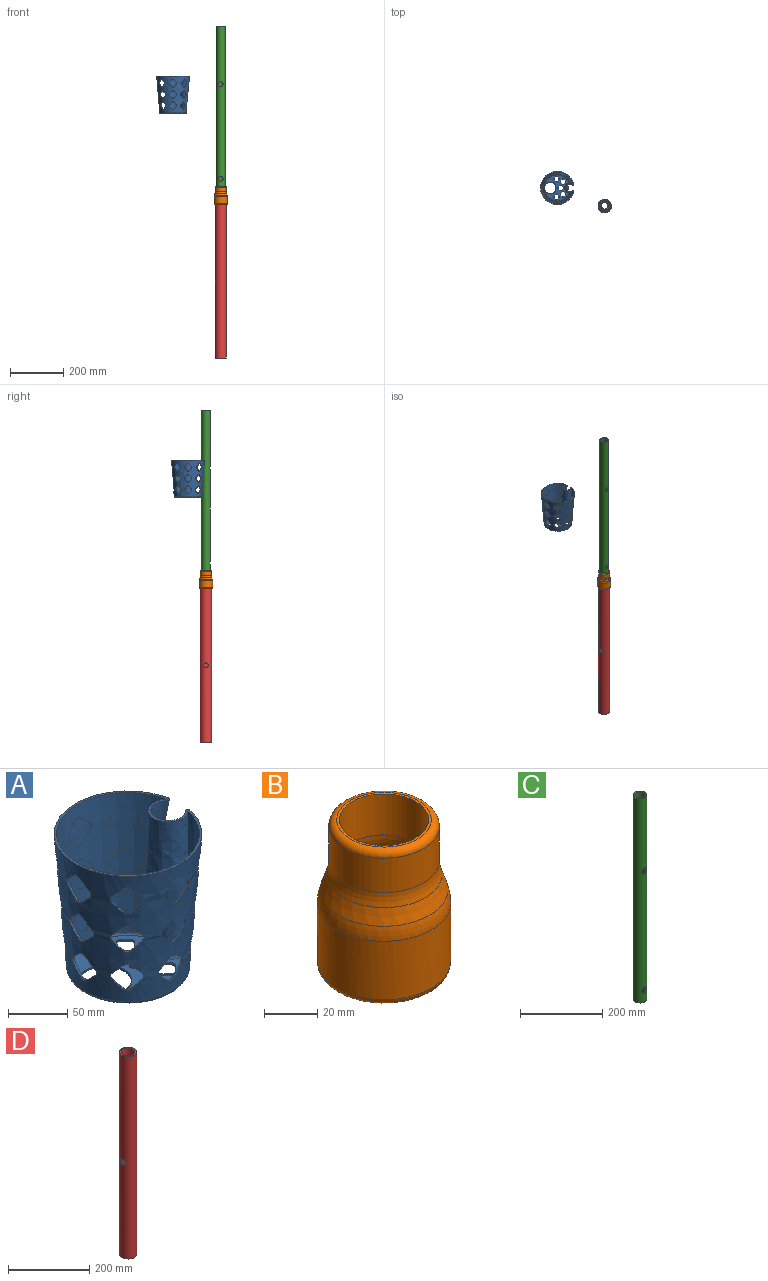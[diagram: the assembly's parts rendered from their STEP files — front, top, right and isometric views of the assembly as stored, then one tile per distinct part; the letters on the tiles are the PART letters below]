
ASSEMBLY  parts=4 mates=2
PART A: 242 faces, bbox 129.3x129x156.7 mm
  f0: plane 97.9x93.66mm, normal (0,0,-1), area 4142.3mm2, adj f1,f2,f3,f4,f5,f6,f7,f8
  f1: plane 7.07x7.07mm, normal (-0.71,-0.71,0), area 20mm2, adj f0,f2,f8,f45
  f2: cylinder r=3mm len=4.24mm, axis (0,0,1), area 9.4mm2, adj f0,f1,f3,f45
  f3: plane 7.07x7.07mm, normal (0.71,-0.71,0), area 20mm2, adj f0,f2,f4,f45
  f4: cylinder r=3mm len=4.24mm, axis (0,0,1), area 9.4mm2, adj f0,f3,f5,f45
  f5: plane 7.07x7.07mm, normal (0.71,0.71,0), area 20mm2, adj f0,f4,f6,f45
  f6: cylinder r=3mm len=4.24mm, axis (0,0,1), area 9.4mm2, adj f0,f5,f7,f45
  f7: plane 7.07x7.07mm, normal (-0.71,0.71,0), area 20mm2, adj f0,f6,f8,f45
  f8: cylinder r=3mm len=4.24mm, axis (0,0,1), area 9.4mm2, adj f0,f1,f7,f45
  f9: plane 7.07x7.07mm, normal (-0.71,-0.71,0), area 20mm2, adj f0,f10,f16,f45
  f10: cylinder r=3mm len=4.24mm, axis (0,0,1), area 9.4mm2, adj f0,f9,f11,f45
  f11: plane 7.07x7.07mm, normal (0.71,-0.71,0), area 20mm2, adj f0,f10,f12,f45
  f12: cylinder r=3mm len=4.24mm, axis (0,0,1), area 9.4mm2, adj f0,f11,f13,f45
  f13: plane 7.07x7.07mm, normal (0.71,0.71,0), area 20mm2, adj f0,f12,f14,f45
  f14: cylinder r=3mm len=4.24mm, axis (0,0,1), area 9.4mm2, adj f0,f13,f15,f45
  f15: plane 7.07x7.07mm, normal (-0.71,0.71,0), area 20mm2, adj f0,f14,f16,f45
  f16: cylinder r=3mm len=4.24mm, axis (0,0,1), area 9.4mm2, adj f0,f9,f15,f45
  f17: plane 7.07x7.07mm, normal (-0.71,-0.71,0), area 20mm2, adj f0,f18,f24,f45
  f18: cylinder r=3mm len=4.24mm, axis (0,0,1), area 9.4mm2, adj f0,f17,f19,f45
  f19: plane 7.07x7.07mm, normal (0.71,-0.71,0), area 20mm2, adj f0,f18,f20,f45
  f20: cylinder r=3mm len=4.24mm, axis (0,0,1), area 9.4mm2, adj f0,f19,f21,f45
  f21: plane 7.07x7.07mm, normal (0.71,0.71,0), area 20mm2, adj f0,f20,f22,f45
  f22: cylinder r=3mm len=4.24mm, axis (0,0,1), area 9.4mm2, adj f0,f21,f23,f45
  f23: plane 7.07x7.07mm, normal (-0.71,0.71,0), area 20mm2, adj f0,f22,f24,f45
  f24: cylinder r=3mm len=4.24mm, axis (0,0,1), area 9.4mm2, adj f0,f17,f23,f45
  f25: torus R=48.95mm, axis (0,0,1), area 1245.7mm2, adj f0,f46,f47,f48
  f26: bspline ~24.16x19.79mm, area 116.1mm2, adj f0,f46,f49,f50,f51,f52
  f27: bspline ~20.75x19.05mm, area 115.6mm2, adj f0,f48,f49,f51,f53,f54
  f28: cylinder r=22mm len=44mm, axis (0,0,1), area 276.5mm2, adj f0,f45
  f29: plane 7.07x7.07mm, normal (-0.71,-0.71,0), area 20mm2, adj f0,f30,f36,f45
  f30: cylinder r=3mm len=4.24mm, axis (0,0,1), area 9.4mm2, adj f0,f29,f31,f45
  f31: plane 7.07x7.07mm, normal (0.71,-0.71,0), area 20mm2, adj f0,f30,f32,f45
  f32: cylinder r=3mm len=4.24mm, axis (0,0,1), area 9.4mm2, adj f0,f31,f33,f45
  f33: plane 7.07x7.07mm, normal (0.71,0.71,0), area 20mm2, adj f0,f32,f34,f45
  f34: cylinder r=3mm len=4.24mm, axis (0,0,1), area 9.4mm2, adj f0,f33,f35,f45
  f35: plane 7.07x7.07mm, normal (-0.71,0.71,0), area 20mm2, adj f0,f34,f36,f45
  f36: cylinder r=3mm len=4.24mm, axis (0,0,1), area 9.4mm2, adj f0,f29,f35,f45
  f37: plane 7.07x7.07mm, normal (-0.71,-0.71,0), area 20mm2, adj f0,f38,f44,f45
  f38: cylinder r=3mm len=4.24mm, axis (0,0,1), area 9.4mm2, adj f0,f37,f39,f45
  f39: plane 7.07x7.07mm, normal (0.71,-0.71,0), area 20mm2, adj f0,f38,f40,f45
  f40: cylinder r=3mm len=4.24mm, axis (0,0,1), area 9.4mm2, adj f0,f39,f41,f45
  f41: plane 7.07x7.07mm, normal (0.71,0.71,0), area 20mm2, adj f0,f40,f42,f45
  f42: cylinder r=3mm len=4.24mm, axis (0,0,1), area 9.4mm2, adj f0,f41,f43,f45
  f43: plane 7.07x7.07mm, normal (-0.71,0.71,0), area 20mm2, adj f0,f42,f44,f45
  f44: cylinder r=3mm len=4.24mm, axis (0,0,1), area 9.4mm2, adj f0,f37,f43,f45
  f45: plane 97.9x93.65mm, normal (0,0,1), area 4142.6mm2, adj f1,f2,f3,f4,f5,f6,f7,f8
  f46: bspline ~3.42x2.81mm, area 7.8mm2, adj f25,f26,f52
  f47: cone r=62.5mm half-angle=4.4deg, axis (0,0,1), area 33496mm2, adj f25,f52,f54,f57,f58,f59,f60,f61
  f48: bspline ~3.42x2.81mm, area 7.8mm2, adj f25,f27,f54
  f49: cylinder r=2.5mm len=14.22mm, axis (1,0,0), area 51.8mm2, adj f26,f27,f50,f53,f228
  f50: plane 12.32x3.76mm, normal (0,-0.71,-0.71), area 56.2mm2, adj f26,f49,f51,f228,f229
  f51: bspline ~140x35.21mm, area 8137.4mm2, adj f26,f27,f50,f53,f57,f58,f59,f229
  f52: bspline ~2.78x2.74mm, area 0.7mm2, adj f26,f46,f47,f58
  f53: plane 12.3x3.77mm, normal (0,0.71,-0.71), area 56.4mm2, adj f27,f49,f51,f228,f230
  f54: bspline ~2.78x2.74mm, area 0.7mm2, adj f27,f47,f48,f57
  f55: torus R=48.95mm, axis (0,0,1), area 405.1mm2, adj f45,f56,f234
  f56: bspline ~40.4x19.74mm, area 89.4mm2, adj f45,f55,f234,f235
  f57: bspline ~152.67x17.18mm, area 590.7mm2, adj f47,f51,f54,f59
  f58: bspline ~145.39x16.58mm, area 590.7mm2, adj f47,f51,f52,f59
  f59: plane 125.53x124.25mm, normal (0,0,1), area 878mm2, adj f47,f51,f57,f58,f234,f235
  f60: cylinder r=5mm len=7.07mm, axis (1,0,0), area 15.8mm2, adj f47,f61,f67,f234
  f61: plane 9.27x9.27mm, normal (0,0.71,-0.71), area 26.6mm2, adj f47,f60,f62,f234
  f62: cylinder r=5mm len=7.07mm, axis (1,0,0), area 16.2mm2, adj f47,f61,f63,f234
  f63: plane 9.32x9.32mm, normal (0,0.71,0.71), area 26.7mm2, adj f47,f62,f64,f234
  f64: cylinder r=5mm len=7.07mm, axis (1,0,0), area 15.8mm2, adj f47,f63,f65,f234
  f65: plane 9.32x9.32mm, normal (0,-0.71,0.71), area 26.7mm2, adj f47,f64,f66,f234
  f66: cylinder r=5mm len=7.07mm, axis (1,0,0), area 16.2mm2, adj f47,f65,f67,f234
  f67: plane 9.27x9.27mm, normal (0,-0.71,-0.71), area 26.6mm2, adj f47,f60,f66,f234
  f68: cylinder r=5mm len=7.07mm, axis (1,0,0), area 15.8mm2, adj f47,f69,f75,f234
  f69: plane 9.27x9.27mm, normal (0,0.71,-0.71), area 26.6mm2, adj f47,f68,f70,f234
  f70: cylinder r=5mm len=7.07mm, axis (1,0,0), area 16.2mm2, adj f47,f69,f71,f234
  f71: plane 9.31x9.31mm, normal (0,0.71,0.71), area 26.6mm2, adj f47,f70,f72,f234
  f72: cylinder r=5mm len=7.07mm, axis (1,0,0), area 15.8mm2, adj f47,f71,f73,f234
  f73: plane 9.31x9.31mm, normal (0,-0.71,0.71), area 26.6mm2, adj f47,f72,f74,f234
  f74: cylinder r=5mm len=7.07mm, axis (1,0,0), area 16.2mm2, adj f47,f73,f75,f234
  f75: plane 9.27x9.27mm, normal (0,-0.71,-0.71), area 26.6mm2, adj f47,f68,f74,f234
  f76: cylinder r=5mm len=7.07mm, axis (1,0,0), area 16.1mm2, adj f47,f77,f83,f234
  f77: plane 9.31x9.31mm, normal (0,0.71,0.71), area 26.6mm2, adj f47,f76,f78,f234
  f78: cylinder r=5mm len=7.07mm, axis (1,0,0), area 15.8mm2, adj f47,f77,f79,f234
  f79: plane 9.31x9.31mm, normal (0,-0.71,0.71), area 26.6mm2, adj f47,f78,f80,f234
  f80: cylinder r=5mm len=7.07mm, axis (1,0,0), area 16.1mm2, adj f47,f79,f81,f234
  f81: plane 9.35x9.35mm, normal (0,-0.71,-0.71), area 26.6mm2, adj f47,f80,f82,f234
  f82: cylinder r=5mm len=7.07mm, axis (1,0,0), area 15.8mm2, adj f47,f81,f83,f234
  f83: plane 9.35x9.35mm, normal (0,0.71,-0.71), area 26.6mm2, adj f47,f76,f82,f234
  f84: cylinder r=5mm len=6.54mm, axis (-0.68,-0.73,0), area 15.8mm2, adj f47,f85,f91,f236
  f85: plane 9.75x9.37mm, normal (0.52,-0.48,-0.71), area 26.6mm2, adj f47,f84,f86,f236
  f86: cylinder r=5mm len=7.07mm, axis (-0.68,-0.73,0), area 16.2mm2, adj f47,f85,f87,f236
  f87: plane 9.32x8.73mm, normal (0.52,-0.48,0.71), area 26.7mm2, adj f47,f86,f88,f236
  f88: cylinder r=5mm len=6.54mm, axis (-0.68,-0.73,0), area 15.8mm2, adj f47,f87,f89,f236
  f89: plane 9.32x8.41mm, normal (-0.52,0.48,0.71), area 26.7mm2, adj f47,f88,f90,f236
  f90: cylinder r=5mm len=7.07mm, axis (-0.68,-0.73,0), area 16.2mm2, adj f47,f89,f91,f236
  f91: plane 9.5x9.37mm, normal (-0.52,0.48,-0.71), area 26.6mm2, adj f47,f84,f90,f236
  f92: cylinder r=5mm len=6.54mm, axis (-0.68,-0.73,0), area 15.8mm2, adj f47,f93,f99,f237
  f93: plane 9.68x9.36mm, normal (0.52,-0.48,-0.71), area 26.6mm2, adj f47,f92,f94,f237
  f94: cylinder r=5mm len=7.07mm, axis (-0.68,-0.73,0), area 16.2mm2, adj f47,f93,f95,f237
  f95: plane 9.31x8.66mm, normal (0.52,-0.48,0.71), area 26.6mm2, adj f47,f94,f96,f237
  f96: cylinder r=5mm len=6.54mm, axis (-0.68,-0.73,0), area 15.8mm2, adj f47,f95,f97,f237
  f97: plane 9.31x8.34mm, normal (-0.52,0.48,0.71), area 26.6mm2, adj f47,f96,f98,f237
  f98: cylinder r=5mm len=7.07mm, axis (-0.68,-0.73,0), area 16.2mm2, adj f47,f97,f99,f237
  f99: plane 9.42x9.36mm, normal (-0.52,0.48,-0.71), area 26.6mm2, adj f47,f92,f98,f237
  f100: cylinder r=5mm len=7.07mm, axis (-0.68,-0.73,0), area 16.1mm2, adj f47,f101,f107,f238
  f101: plane 9.31x8.6mm, normal (0.52,-0.48,0.71), area 26.6mm2, adj f47,f100,f102,f238
  f102: cylinder r=5mm len=6.54mm, axis (-0.68,-0.73,0), area 15.8mm2, adj f47,f101,f103,f238
  f103: plane 9.31x8.27mm, normal (-0.52,0.48,0.71), area 26.6mm2, adj f47,f102,f104,f238
  f104: cylinder r=5mm len=7.07mm, axis (-0.68,-0.73,0), area 16.1mm2, adj f47,f103,f105,f238
  f105: plane 9.36x9.36mm, normal (-0.52,0.48,-0.71), area 26.6mm2, adj f47,f104,f106,f238
  f106: cylinder r=5mm len=6.54mm, axis (-0.68,-0.73,0), area 15.8mm2, adj f47,f105,f107,f238
  f107: plane 9.61x9.36mm, normal (0.52,-0.48,-0.71), area 26.6mm2, adj f47,f100,f106,f238
  f108: cylinder r=5mm len=7.12mm, axis (0.02,-1,0), area 15.8mm2, adj f47,f109,f115,f239
  f109: plane 9.37x9.37mm, normal (0.71,0.02,-0.71), area 26.6mm2, adj f47,f108,f110,f239
  f110: cylinder r=5mm len=7.07mm, axis (0.02,-1,0), area 16.2mm2, adj f47,f109,f111,f239
  f111: plane 9.35x9.32mm, normal (0.71,0.02,0.71), area 26.7mm2, adj f47,f110,f112,f239
  f112: cylinder r=5mm len=7.12mm, axis (0.02,-1,0), area 15.8mm2, adj f47,f111,f113,f239
  f113: plane 9.38x9.32mm, normal (-0.71,-0.02,0.71), area 26.7mm2, adj f47,f112,f114,f239
  f114: cylinder r=5mm len=7.07mm, axis (0.02,-1,0), area 16.2mm2, adj f47,f113,f115,f239
  f115: plane 9.47x9.37mm, normal (-0.71,-0.02,-0.71), area 26.6mm2, adj f47,f108,f114,f239
  f116: cylinder r=5mm len=7.12mm, axis (0.02,-1,0), area 15.8mm2, adj f47,f117,f123,f240
  f117: plane 9.36x9.36mm, normal (0.71,0.02,-0.71), area 26.6mm2, adj f47,f116,f118,f240
  f118: cylinder r=5mm len=7.07mm, axis (0.02,-1,0), area 16.2mm2, adj f47,f117,f119,f240
  f119: plane 9.34x9.31mm, normal (0.71,0.02,0.71), area 26.6mm2, adj f47,f118,f120,f240
  f120: cylinder r=5mm len=7.12mm, axis (0.02,-1,0), area 15.8mm2, adj f47,f119,f121,f240
  f121: plane 9.37x9.31mm, normal (-0.71,-0.02,0.71), area 26.6mm2, adj f47,f120,f122,f240
  f122: cylinder r=5mm len=7.07mm, axis (0.02,-1,0), area 16.2mm2, adj f47,f121,f123,f240
  f123: plane 9.46x9.36mm, normal (-0.71,-0.02,-0.71), area 26.6mm2, adj f47,f116,f122,f240
  f124: cylinder r=5mm len=7.07mm, axis (0.02,-1,0), area 16.1mm2, adj f47,f125,f131,f241
  f125: plane 9.34x9.31mm, normal (0.71,0.02,0.71), area 26.6mm2, adj f47,f124,f126,f241
  f126: cylinder r=5mm len=7.12mm, axis (0.02,-1,0), area 15.8mm2, adj f47,f125,f127,f241
  f127: plane 9.37x9.31mm, normal (-0.71,-0.02,0.71), area 26.6mm2, adj f47,f126,f128,f241
  f128: cylinder r=5mm len=7.07mm, axis (0.02,-1,0), area 16.1mm2, adj f47,f127,f129,f241
  f129: plane 9.45x9.36mm, normal (-0.71,-0.02,-0.71), area 26.6mm2, adj f47,f128,f130,f241
  f130: cylinder r=5mm len=7.12mm, axis (0.02,-1,0), area 15.8mm2, adj f47,f129,f131,f241
  f131: plane 9.36x9.35mm, normal (0.71,0.02,-0.71), area 26.6mm2, adj f47,f124,f130,f241
  f132: cylinder r=5mm len=6.46mm, axis (0.72,-0.7,0), area 15.8mm2, adj f47,f133,f139,f234
  f133: plane 9.57x9.27mm, normal (0.49,0.51,-0.71), area 26.6mm2, adj f47,f132,f134,f234
  f134: cylinder r=5mm len=7.07mm, axis (0.72,-0.7,0), area 16.2mm2, adj f47,f133,f135,f234
  f135: plane 9.32x8.63mm, normal (0.49,0.51,0.71), area 26.7mm2, adj f47,f134,f136,f234
  f136: cylinder r=5mm len=6.46mm, axis (0.72,-0.7,0), area 15.8mm2, adj f47,f135,f137,f234
  f137: plane 9.32x8.52mm, normal (-0.49,-0.51,0.71), area 26.7mm2, adj f47,f136,f138,f234
  f138: cylinder r=5mm len=7.07mm, axis (0.72,-0.7,0), area 16.2mm2, adj f47,f137,f139,f234
  f139: plane 9.48x9.27mm, normal (-0.49,-0.51,-0.71), area 26.6mm2, adj f47,f132,f138,f234
  f140: cylinder r=5mm len=6.46mm, axis (0.72,-0.7,0), area 15.8mm2, adj f47,f141,f147,f234
  f141: plane 9.5x9.27mm, normal (0.49,0.51,-0.71), area 26.6mm2, adj f47,f140,f142,f234
  f142: cylinder r=5mm len=7.07mm, axis (0.72,-0.7,0), area 16.2mm2, adj f47,f141,f143,f234
  f143: plane 9.31x8.56mm, normal (0.49,0.51,0.71), area 26.6mm2, adj f47,f142,f144,f234
  f144: cylinder r=5mm len=6.46mm, axis (0.72,-0.7,0), area 15.8mm2, adj f47,f143,f145,f234
  f145: plane 9.31x8.45mm, normal (-0.49,-0.51,0.71), area 26.6mm2, adj f47,f144,f146,f234
  f146: cylinder r=5mm len=7.07mm, axis (0.72,-0.7,0), area 16.2mm2, adj f47,f145,f147,f234
  f147: plane 9.42x9.27mm, normal (-0.49,-0.51,-0.71), area 26.6mm2, adj f47,f140,f146,f234
  f148: cylinder r=5mm len=7.07mm, axis (0.72,-0.7,0), area 16.1mm2, adj f47,f149,f155,f234
  f149: plane 9.31x8.5mm, normal (0.49,0.51,0.71), area 26.6mm2, adj f47,f148,f150,f234
  f150: cylinder r=5mm len=6.46mm, axis (0.72,-0.7,0), area 15.8mm2, adj f47,f149,f151,f234
  f151: plane 9.31x8.39mm, normal (-0.49,-0.51,0.71), area 26.6mm2, adj f47,f150,f152,f234
  f152: cylinder r=5mm len=7.07mm, axis (0.72,-0.7,0), area 16.1mm2, adj f47,f151,f153,f234
  f153: plane 9.44x9.35mm, normal (-0.49,-0.51,-0.71), area 26.6mm2, adj f47,f152,f154,f234
  f154: cylinder r=5mm len=6.46mm, axis (0.72,-0.7,0), area 15.8mm2, adj f47,f153,f155,f234
  f155: plane 9.53x9.35mm, normal (0.49,0.51,-0.71), area 26.6mm2, adj f47,f148,f154,f234
  f156: cylinder r=5mm len=6.46mm, axis (0.72,0.7,0), area 15.8mm2, adj f47,f157,f163,f234
  f157: plane 9.48x9.27mm, normal (-0.49,0.51,-0.71), area 26.6mm2, adj f47,f156,f158,f234
  f158: cylinder r=5mm len=7.07mm, axis (0.72,0.7,0), area 16.2mm2, adj f47,f157,f159,f234
  f159: plane 9.32x8.52mm, normal (-0.49,0.51,0.71), area 26.7mm2, adj f47,f158,f160,f234
  f160: cylinder r=5mm len=6.46mm, axis (0.72,0.7,0), area 15.8mm2, adj f47,f159,f161,f234
  f161: plane 9.32x8.63mm, normal (0.49,-0.51,0.71), area 26.7mm2, adj f47,f160,f162,f234
  f162: cylinder r=5mm len=7.07mm, axis (0.72,0.7,0), area 16.2mm2, adj f47,f161,f163,f234
  f163: plane 9.57x9.27mm, normal (0.49,-0.51,-0.71), area 26.6mm2, adj f47,f156,f162,f234
  f164: cylinder r=5mm len=6.46mm, axis (0.72,0.7,0), area 15.8mm2, adj f47,f165,f171,f234
  f165: plane 9.42x9.27mm, normal (-0.49,0.51,-0.71), area 26.6mm2, adj f47,f164,f166,f234
  f166: cylinder r=5mm len=7.07mm, axis (0.72,0.7,0), area 16.2mm2, adj f47,f165,f167,f234
  f167: plane 9.31x8.45mm, normal (-0.49,0.51,0.71), area 26.6mm2, adj f47,f166,f168,f234
  f168: cylinder r=5mm len=6.46mm, axis (0.72,0.7,0), area 15.8mm2, adj f47,f167,f169,f234
  f169: plane 9.31x8.56mm, normal (0.49,-0.51,0.71), area 26.6mm2, adj f47,f168,f170,f234
  f170: cylinder r=5mm len=7.07mm, axis (0.72,0.7,0), area 16.2mm2, adj f47,f169,f171,f234
  f171: plane 9.5x9.27mm, normal (0.49,-0.51,-0.71), area 26.6mm2, adj f47,f164,f170,f234
  f172: cylinder r=5mm len=7.07mm, axis (0.72,0.7,0), area 16.1mm2, adj f47,f173,f179,f234
  f173: plane 9.31x8.39mm, normal (-0.49,0.51,0.71), area 26.6mm2, adj f47,f172,f174,f234
  f174: cylinder r=5mm len=6.46mm, axis (0.72,0.7,0), area 15.8mm2, adj f47,f173,f175,f234
  f175: plane 9.31x8.5mm, normal (0.49,-0.51,0.71), area 26.6mm2, adj f47,f174,f176,f234
  f176: cylinder r=5mm len=7.07mm, axis (0.72,0.7,0), area 16.1mm2, adj f47,f175,f177,f234
  f177: plane 9.53x9.35mm, normal (0.49,-0.51,-0.71), area 26.6mm2, adj f47,f176,f178,f234
  f178: cylinder r=5mm len=6.46mm, axis (0.72,0.7,0), area 15.8mm2, adj f47,f177,f179,f234
  f179: plane 9.44x9.35mm, normal (-0.49,0.51,-0.71), area 26.6mm2, adj f47,f172,f178,f234
  f180: cylinder r=5mm len=7.12mm, axis (0.02,1,0), area 15.8mm2, adj f47,f181,f187,f234
  f181: plane 9.37x9.27mm, normal (-0.71,0.02,-0.71), area 26.6mm2, adj f47,f180,f182,f234
  f182: cylinder r=5mm len=7.07mm, axis (0.02,1,0), area 16.2mm2, adj f47,f181,f183,f234
  f183: plane 9.38x9.32mm, normal (-0.71,0.02,0.71), area 26.7mm2, adj f47,f182,f184,f234
  f184: cylinder r=5mm len=7.12mm, axis (0.02,1,0), area 15.8mm2, adj f47,f183,f185,f234
  f185: plane 9.35x9.32mm, normal (0.71,-0.02,0.71), area 26.7mm2, adj f47,f184,f186,f234
  f186: cylinder r=5mm len=7.07mm, axis (0.02,1,0), area 16.2mm2, adj f47,f185,f187,f234
  f187: plane 9.27x9.26mm, normal (0.71,-0.02,-0.71), area 26.6mm2, adj f47,f180,f186,f234
  f188: cylinder r=5mm len=7.12mm, axis (0.02,1,0), area 15.8mm2, adj f47,f189,f195,f234
  f189: plane 9.36x9.27mm, normal (-0.71,0.02,-0.71), area 26.6mm2, adj f47,f188,f190,f234
  f190: cylinder r=5mm len=7.07mm, axis (0.02,1,0), area 16.2mm2, adj f47,f189,f191,f234
  f191: plane 9.37x9.31mm, normal (-0.71,0.02,0.71), area 26.6mm2, adj f47,f190,f192,f234
  f192: cylinder r=5mm len=7.12mm, axis (0.02,1,0), area 15.8mm2, adj f47,f191,f193,f234
  f193: plane 9.34x9.31mm, normal (0.71,-0.02,0.71), area 26.6mm2, adj f47,f192,f194,f234
  f194: cylinder r=5mm len=7.07mm, axis (0.02,1,0), area 16.2mm2, adj f47,f193,f195,f234
  f195: plane 9.27x9.27mm, normal (0.71,-0.02,-0.71), area 26.6mm2, adj f47,f188,f194,f234
  f196: cylinder r=5mm len=7.07mm, axis (0.02,1,0), area 16.1mm2, adj f47,f197,f203,f234
  f197: plane 9.37x9.31mm, normal (-0.71,0.02,0.71), area 26.6mm2, adj f47,f196,f198,f234
  f198: cylinder r=5mm len=7.12mm, axis (0.02,1,0), area 15.8mm2, adj f47,f197,f199,f234
  f199: plane 9.34x9.31mm, normal (0.71,-0.02,0.71), area 26.6mm2, adj f47,f198,f200,f234
  f200: cylinder r=5mm len=7.07mm, axis (0.02,1,0), area 16.1mm2, adj f47,f199,f201,f234
  f201: plane 9.35x9.35mm, normal (0.71,-0.02,-0.71), area 26.6mm2, adj f47,f200,f202,f234
  f202: cylinder r=5mm len=7.12mm, axis (0.02,1,0), area 15.8mm2, adj f47,f201,f203,f234
  f203: plane 9.44x9.35mm, normal (-0.71,0.02,-0.71), area 26.6mm2, adj f47,f196,f202,f234
  f204: cylinder r=5mm len=6.54mm, axis (-0.68,0.73,0), area 15.8mm2, adj f47,f205,f211,f234
  f205: plane 9.39x9.27mm, normal (-0.52,-0.48,-0.71), area 26.6mm2, adj f47,f204,f206,f234
  f206: cylinder r=5mm len=7.07mm, axis (-0.68,0.73,0), area 16.2mm2, adj f47,f205,f207,f234
  f207: plane 9.32x8.41mm, normal (-0.52,-0.48,0.71), area 26.7mm2, adj f47,f206,f208,f234
  f208: cylinder r=5mm len=6.54mm, axis (-0.68,0.73,0), area 15.8mm2, adj f47,f207,f209,f234
  f209: plane 9.32x8.73mm, normal (0.52,0.48,0.71), area 26.7mm2, adj f47,f208,f210,f234
  f210: cylinder r=5mm len=7.07mm, axis (-0.68,0.73,0), area 16.2mm2, adj f47,f209,f211,f234
  f211: plane 9.64x9.27mm, normal (0.52,0.48,-0.71), area 26.6mm2, adj f47,f204,f210,f234
  f212: cylinder r=5mm len=6.54mm, axis (-0.68,0.73,0), area 15.8mm2, adj f47,f213,f219,f234
  f213: plane 9.33x9.27mm, normal (-0.52,-0.48,-0.71), area 26.6mm2, adj f47,f212,f214,f234
  f214: cylinder r=5mm len=7.07mm, axis (-0.68,0.73,0), area 16.2mm2, adj f47,f213,f215,f234
  f215: plane 9.31x8.34mm, normal (-0.52,-0.48,0.71), area 26.6mm2, adj f47,f214,f216,f234
  f216: cylinder r=5mm len=6.54mm, axis (-0.68,0.73,0), area 15.8mm2, adj f47,f215,f217,f234
  f217: plane 9.31x8.66mm, normal (0.52,0.48,0.71), area 26.6mm2, adj f47,f216,f218,f234
  f218: cylinder r=5mm len=7.07mm, axis (-0.68,0.73,0), area 16.2mm2, adj f47,f217,f219,f234
  f219: plane 9.58x9.27mm, normal (0.52,0.48,-0.71), area 26.6mm2, adj f47,f212,f218,f234
  f220: cylinder r=5mm len=7.07mm, axis (-0.68,0.73,0), area 16.1mm2, adj f47,f221,f227,f234
  f221: plane 9.31x8.27mm, normal (-0.52,-0.48,0.71), area 26.6mm2, adj f47,f220,f222,f234
  f222: cylinder r=5mm len=6.54mm, axis (-0.68,0.73,0), area 15.8mm2, adj f47,f221,f223,f234
  f223: plane 9.31x8.6mm, normal (0.52,0.48,0.71), area 26.6mm2, adj f47,f222,f224,f234
  f224: cylinder r=5mm len=7.07mm, axis (-0.68,0.73,0), area 16.1mm2, adj f47,f223,f225,f234
  f225: plane 9.61x9.35mm, normal (0.52,0.48,-0.71), area 26.6mm2, adj f47,f224,f226,f234
  f226: cylinder r=5mm len=6.54mm, axis (-0.68,0.73,0), area 15.8mm2, adj f47,f225,f227,f234
  f227: plane 9.35x9.35mm, normal (-0.52,-0.48,-0.71), area 26.6mm2, adj f47,f220,f226,f234
  f228: plane 12.24x12.24mm, normal (1,0,0), area 97mm2, adj f49,f50,f53,f229,f230,f231,f232,f233
  f229: cylinder r=2.5mm len=10.41mm, axis (1,0,0), area 40.8mm2, adj f50,f51,f228,f233
  f230: cylinder r=2.5mm len=10.35mm, axis (1,0,0), area 40.6mm2, adj f51,f53,f228,f231
  f231: plane 11.19x3.64mm, normal (0,0.71,0.71), area 55.2mm2, adj f51,f228,f230,f232
  f232: cylinder r=2.5mm len=11.18mm, axis (1,0,0), area 43.9mm2, adj f51,f228,f231,f233
  f233: plane 11.21x3.67mm, normal (0,-0.71,0.71), area 55.8mm2, adj f51,f228,f229,f232
  f234: cone r=60.51mm half-angle=4.4deg, axis (0,0,1), area 35002mm2, adj f55,f56,f59,f60,f61,f62,f63,f64
  f235: offset ~144x39.21mm, area 9571.8mm2, adj f56,f59,f234
  f236: cone r=60.51mm half-angle=4.4deg, axis (0,0,1), area 504.7mm2, adj f84,f85,f86,f87,f88,f89,f90,f91
  f237: cone r=60.51mm half-angle=4.4deg, axis (0,0,1), area 504.1mm2, adj f92,f93,f94,f95,f96,f97,f98,f99
  f238: cone r=60.51mm half-angle=4.4deg, axis (0,0,1), area 503.7mm2, adj f100,f101,f102,f103,f104,f105,f106,f107
  f239: cone r=60.51mm half-angle=4.4deg, axis (0,0,1), area 504.7mm2, adj f108,f109,f110,f111,f112,f113,f114,f115
  f240: cone r=60.51mm half-angle=4.4deg, axis (0,0,1), area 504.1mm2, adj f116,f117,f118,f119,f120,f121,f122,f123
  f241: cone r=60.51mm half-angle=4.4deg, axis (0,0,1), area 503.7mm2, adj f124,f125,f126,f127,f128,f129,f130,f131
PART B: 14 faces, bbox 57.5x57.5x68 mm
  f0: cylinder r=21mm len=42mm, axis (0,0,1), area 3933.8mm2, adj f1,f11
  f1: plane 44x44mm, normal (0,0,-1), area 135.1mm2, adj f0,f12
  f2: cylinder r=25mm len=50mm, axis (0,0,1), area 4211.9mm2, adj f3,f12
  f3: torus R=5mm, axis (0,0,1), area 979.5mm2, adj f2,f4
  f4: cone r=21.74mm half-angle=18.1deg, axis (0,0,-1), area 1049.9mm2, adj f3,f5
  f5: torus R=40.75mm, axis (0,0,1), area 837mm2, adj f4,f6
  f6: cylinder r=20.75mm len=41.5mm, axis (0,0,1), area 2061.7mm2, adj f5,f13
  f7: plane 35.5x35.5mm, normal (0,0,1), area 108.4mm2, adj f8,f13
  f8: cylinder r=16.75mm len=33.5mm, axis (0,0,1), area 1980mm2, adj f7,f9
  f9: torus R=36.75mm, axis (0,0,1), area 678.2mm2, adj f8,f10
  f10: cone r=20.01mm half-angle=18.1deg, axis (0,0,-1), area 866.3mm2, adj f9,f11
  f11: torus R=1mm, axis (0,0,1), area 820.7mm2, adj f0,f10
  f12: torus R=22mm, axis (0,0,-1), area 707.9mm2, adj f1,f2
  f13: torus R=17.75mm, axis (0,0,1), area 582.1mm2, adj f6,f7
PART C: 6 faces, bbox 33.5x33.5x609.6 mm
  f0: cylinder r=12.75mm len=609.6mm, axis (0,0,1), area 48287.2mm2, adj f2,f3,f4,f5
  f1: cylinder r=16.75mm len=609.6mm, axis (0,0,1), area 63626.6mm2, adj f2,f3,f4,f5
  f2: plane 33.5x33.5mm, normal (0,0,1), area 370.7mm2, adj f0,f1
  f3: plane 33.5x33.5mm, normal (0,0,-1), area 370.7mm2, adj f0,f1
  f4: cylinder r=9mm len=18mm, axis (0,1,0), area 254.2mm2, adj f0,f1
  f5: cylinder r=9mm len=18mm, axis (0,1,0), area 254.2mm2, adj f0,f1
PART D: 5 faces, bbox 42x42x609.6 mm
  f0: cylinder r=21mm len=609.6mm, axis (0,0,1), area 80174.4mm2, adj f1,f3,f4
  f1: plane 42x42mm, normal (0,0,1), area 477.5mm2, adj f0,f2
  f2: cylinder r=17mm len=609.6mm, axis (0,0,1), area 64849.5mm2, adj f1,f3,f4
  f3: plane 42x42mm, normal (0,0,-1), area 477.5mm2, adj f0,f2
  f4: cylinder r=9mm len=18mm, axis (1,0,0), area 240.9mm2, adj f0,f2
PLACE A t=(-234.98,194.17,564.24)mm
PLACE B t=(-57.18,126.97,115.59)mm
PLACE C t=(-57.18,127,433.63)mm
PLACE D t=(-57.18,126.97,-155.57)mm
MATE slider B.f0 <-> D.f0  axis (0,0,-1) through (-57.18,126.97,84.68)mm
MATE slider B.f0 <-> C.f0  axis (0,0,1) through (-57.18,126.97,149.68)mm
